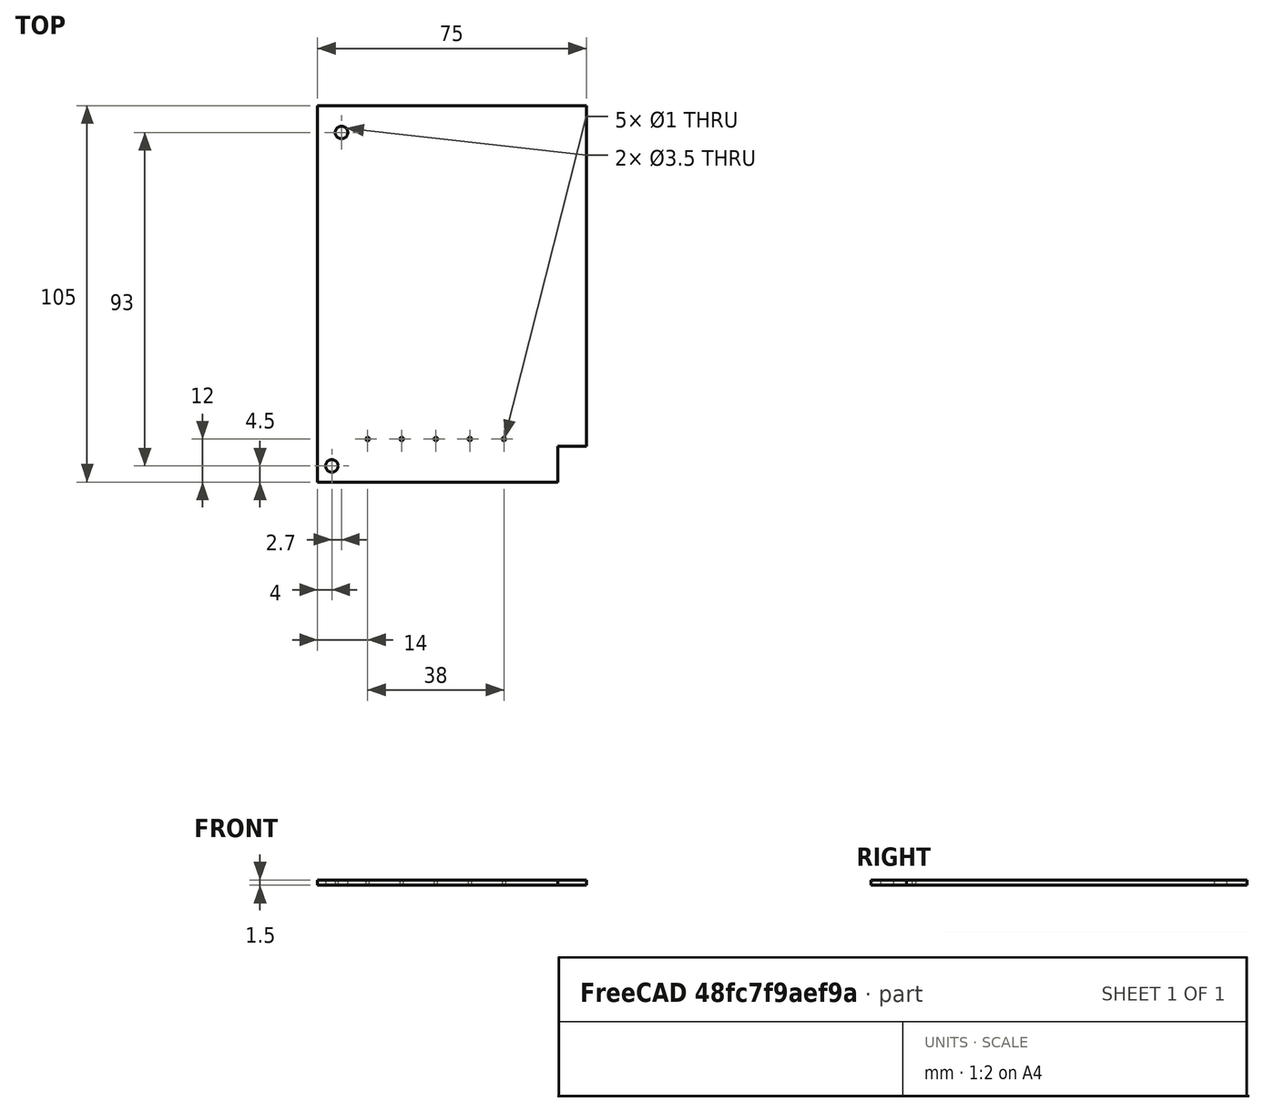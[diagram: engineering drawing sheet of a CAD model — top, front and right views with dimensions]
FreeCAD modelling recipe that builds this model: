
FCSTD DOCUMENT  (FreeCAD 0.19R23058 (Git))
Label: board
License: All rights reserved
LicenseURL: http://en.wikipedia.org/wiki/All_rights_reserved
objects: PartDesign::Line×2, Sketcher::SketchObject×1, PartDesign::Pad×1, PartDesign::Body×1
note: 6 computed .brp shape members not serialized (recipe doc carries the construction recipe); baked Part::Feature solids carry a one-line shape summary decoded from their .brp

FEATURE [Sketcher::SketchObject] Sketch
  MapMode = 5
  Support = -> [XY_Plane]
  sketch-geometry (17):
    g0: LineSegment StartX=-37.5 StartY=52.5 StartZ=0 EndX=37.5 EndY=52.5 EndZ=0
    g1: LineSegment StartX=37.5 StartY=52.5 StartZ=0 EndX=37.5 EndY=-42.5 EndZ=0
    g2: LineSegment StartX=29.5 StartY=-52.5 StartZ=0 EndX=-37.5 EndY=-52.5 EndZ=0
    g3: LineSegment StartX=-37.5 StartY=-52.5 StartZ=0 EndX=-37.5 EndY=52.5 EndZ=0
    g4: Circle CenterX=-33.5 CenterY=-48 CenterZ=0 NormalX=0 NormalY=0 NormalZ=1 AngleXU=0 Radius=1.75
    g5: Circle CenterX=-30.8 CenterY=45 CenterZ=0 NormalX=0 NormalY=0 NormalZ=1 AngleXU=0 Radius=1.75
    g6: LineSegment StartX=29.5 StartY=-52.5 StartZ=0 EndX=29.5 EndY=-42.5 EndZ=0
    g7: LineSegment StartX=29.5 StartY=-42.5 StartZ=0 EndX=37.5 EndY=-42.5 EndZ=0
    g8: LineSegment [constr] StartX=-23.5 StartY=-40.5 StartZ=0 EndX=-14 EndY=-40.5 EndZ=0
    g9: LineSegment [constr] StartX=-14 StartY=-40.5 StartZ=0 EndX=-4.5 EndY=-40.5 EndZ=0
    g10: LineSegment [constr] StartX=-4.5 StartY=-40.5 StartZ=0 EndX=5 EndY=-40.5 EndZ=0
    g11: LineSegment [constr] StartX=5 StartY=-40.5 StartZ=0 EndX=14.5 EndY=-40.5 EndZ=0
    g12: Circle CenterX=-23.5 CenterY=-40.5 CenterZ=0 NormalX=0 NormalY=0 NormalZ=1 AngleXU=0 Radius=0.5
    g13: Circle CenterX=-14 CenterY=-40.5 CenterZ=0 NormalX=0 NormalY=0 NormalZ=1 AngleXU=0 Radius=0.5
    g14: Circle CenterX=-4.5 CenterY=-40.5 CenterZ=0 NormalX=0 NormalY=0 NormalZ=1 AngleXU=0 Radius=0.5
    g15: Circle CenterX=5 CenterY=-40.5 CenterZ=0 NormalX=0 NormalY=0 NormalZ=1 AngleXU=0 Radius=0.5
    g16: Circle CenterX=14.5 CenterY=-40.5 CenterZ=0 NormalX=0 NormalY=0 NormalZ=1 AngleXU=0 Radius=0.5
  constraints (45):
    c: Coincident(g0,g1)
    c: Coincident(g2,g3)
    c: Coincident(g3,g0)
    c: Horizontal(g2)
    c: Vertical(g1)
    c: Symmetric(g0,g2,g-1)
    c: Symmetric(g0,g0,g-2)
    c: DistanceY(g3,g3) = 105
    c: Coincident(g2,g6)
    c: Coincident(g6,g7)
    c: Coincident(g7,g1)
    c: Horizontal(g7)
    c: Vertical(g6)
    c: DistanceX(g0,g0) = 75
    c: DistanceY(g6,g6) = 10
    c: DistanceX(g7,g7) = 8
    c: Radius(g4) = 1.75
    c: Equal(g4,g5)
    c: DistanceY(g2,g4) = 4.5
    c: DistanceX(g2,g4) = 4
    c: DistanceY(g5,g0) = 7.5
    c: DistanceX(g0,g5) = 6.7
    c: Horizontal(g8)
    c: Coincident(g8,g9)
    c: Horizontal(g9)
    c: Coincident(g9,g10)
    c: Horizontal(g10)
    c: Coincident(g10,g11)
    c: Horizontal(g11)
    c: DistanceX(g8,g8) = 9.5
    c: Equal(g8,g9)
    c: Equal(g9,g10)
    c: Equal(g10,g11)
    c: DistanceY(g2,g8) = 12
    c: DistanceX(g2,g8) = 14
    c: Coincident(g12,g8)
    c: Coincident(g13,g8)
    c: Coincident(g14,g9)
    c: Coincident(g15,g10)
    c: Coincident(g16,g11)
    c: Radius(g16) = 0.5
    c: Equal(g16,g15)
    c: Equal(g15,g14)
    c: Equal(g14,g13)
    c: Equal(g13,g12)
FEATURE [PartDesign::Pad] Pad
  Direction = (1,1,1)
  Length = 1.5
  Length2 = 100
  Profile = -> Sketch
  Type = 0
FEATURE [PartDesign::Line] HoleAxis_1  label="Fastnr_1"
  AttacherType = Attacher::AttachEngineLine
  Length = 4.93174
  MapMode = 19
  Placement = pos=(-33.5,-48,0) rot=(0,0,1;0rad)
  ResizeMode = 1
  Support = -> [Pad]
FEATURE [PartDesign::Line] HoleAxis_2  label="Contact_1"
  AttacherType = Attacher::AttachEngineLine
  Length = 1.40907
  MapMode = 19
  Placement = pos=(-23.5,-40.5,1.5) rot=(0,0,1;0rad)
  ResizeMode = 1
  Support = -> [Pad]
FEATURE [PartDesign::Body] Body
  Group = -> [Sketch,Pad,HoleAxis_1,HoleAxis_2]
  Origin = -> Origin
  Tip = -> Pad
